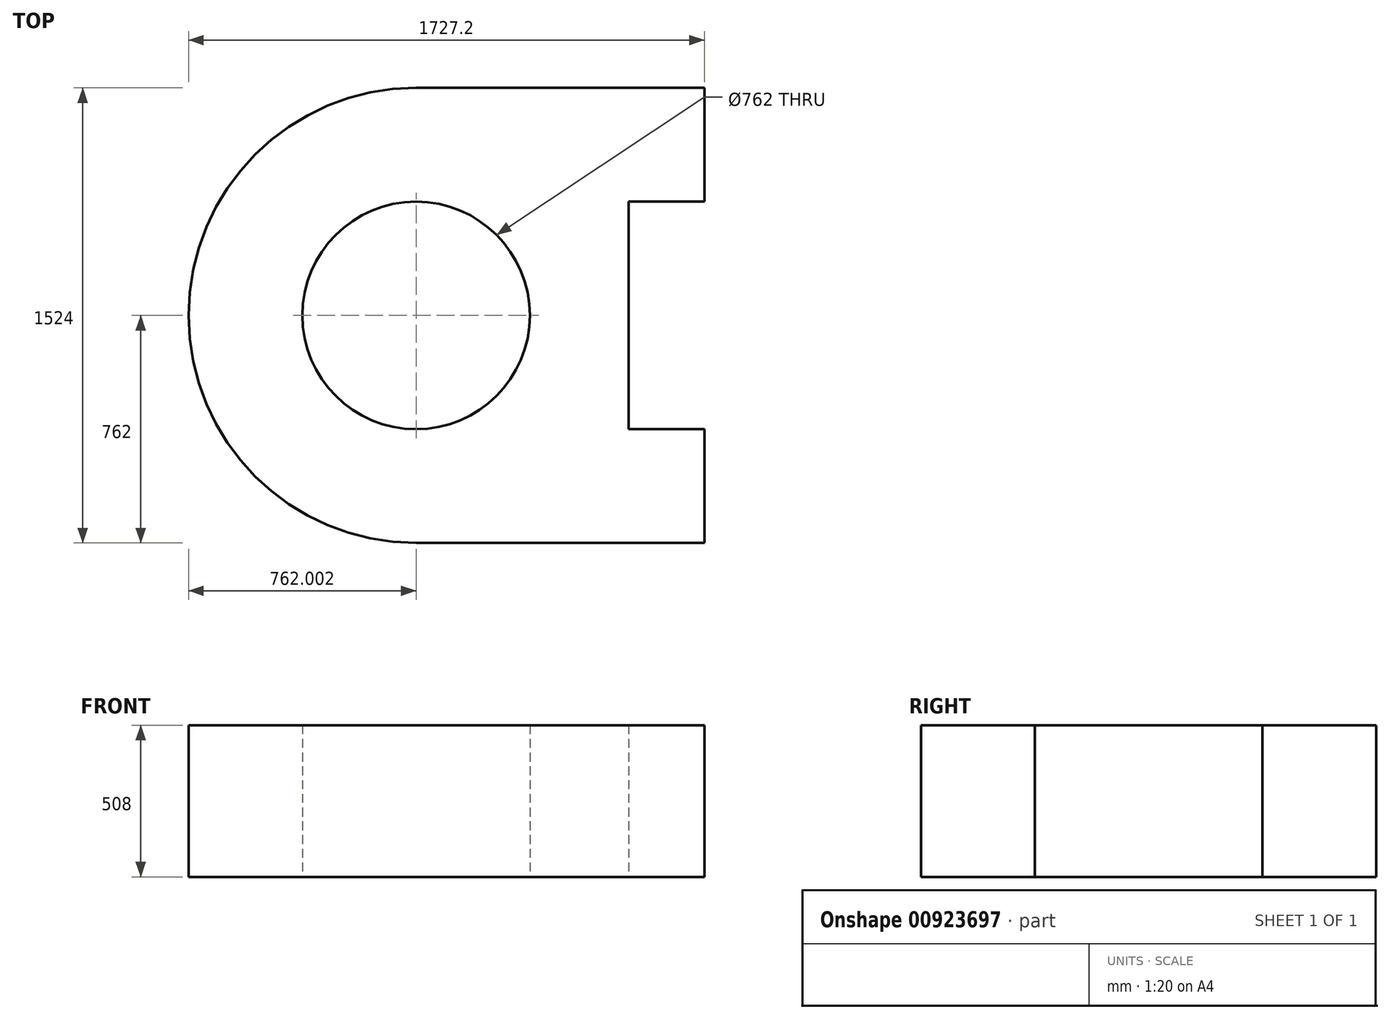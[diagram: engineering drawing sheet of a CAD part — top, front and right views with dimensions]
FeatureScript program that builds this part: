
annotation { "Feature Type Name" : "Feature", "Feature Type Description" : "" }
export const myFeature = defineFeature(function(context is Context, id is Id, definition is map)
    precondition{}
    {
        {
            var Q0;
            Q0=qCreatedBy(makeId("Top.planeOp"),FACE);
            var sketch = newSketch(context, id + "F0", { "sketchPlane" : qUnion([Q0])});
            skLineSegment(sketch, "E0", {"start": v(-543.23, 1143) * mm, "end": v(421.97, 1143) * mm});
            skLineSegment(sketch, "E1", {"start": v(421.97, 1143) * mm, "end": v(421.97, 762) * mm});
            skLineSegment(sketch, "E2", {"start": v(421.97, 762) * mm, "end": v(167.97, 762) * mm});
            skLineSegment(sketch, "E3", {"start": v(167.97, 762) * mm, "end": v(167.97, 0) * mm});
            skLineSegment(sketch, "E4", {"start": v(167.97, 0) * mm, "end": v(421.97, 0) * mm});
            skLineSegment(sketch, "E5", {"start": v(421.97, 0) * mm, "end": v(421.97, -381) * mm});
            skLineSegment(sketch, "E6", {"start": v(421.97, -381) * mm, "end": v(-543.23, -381) * mm});
            skArc(sketch, "E7", {"start": v(-543.23, 1143) * mm, "mid": v(-1305.23, 381) * mm, "end": v(-543.23, -381) * mm});
            skCircle(sketch, "E8", {"center": v(-543.23, 381) * mm, "radius": 381 * mm});
            skSolve(sketch);
        }
        {
            var Q0;
            Q0=makeQuery(id+"F0.imprint","IMPRINT",FACE,{"disambiguationData":[TD([[makeQuery(id+"F0.imprint","IMPRINT",EDGE,{"derivedFrom":sQuery(id+"F0.wireOp",EDGE,"E0")}),-1.0]])]});
            extrude(context, id + "F1", {"entities" : qUnion([Q0]), "depth" : 508 * mm, "offsetDistance" : 25.4 * mm});
        }
    });
